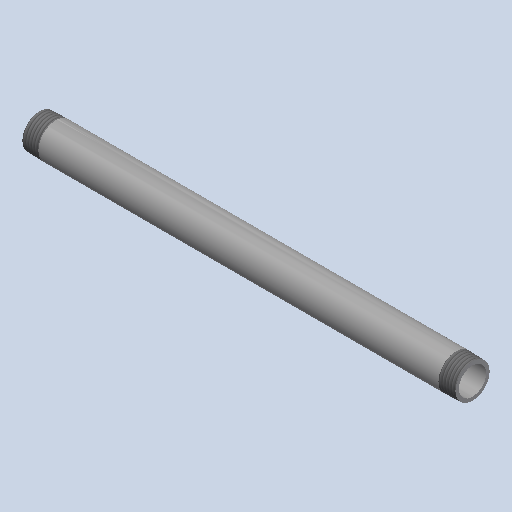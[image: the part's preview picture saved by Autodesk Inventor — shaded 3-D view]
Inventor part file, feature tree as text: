
AUTODESK INVENTOR PART (.ipt)
format: ipt  version: 2025 (Build 290162000, 162)  size: 179,712 bytes
history: native  units: mm (DEFAULTED — no unit token found)
features: other x8, revolve x1
ambient origin geometry x8: Origin, YZ Plane, XZ Plane, XY Plane, X Axis, Y Axis, Z Axis, Center Point
bodies: Solid1 (feature_tree)
feature tree (9):
  revolve  "Revolution1"  [1 undecoded]
  other  "Work Axis1"
  other  "Work Point5"
  other  "Work Axis2"
  other  "Work Point6"
  other  "Work Axis3"
  other  "Work Axis4"
  other  "Work Point7"
  other  "Work Point8"
note: 1 required parameter value undecoded (feature->parameter linkage not recoverable at this tier; creation-order binding heuristic only, values carry confidence <= 0.55)
